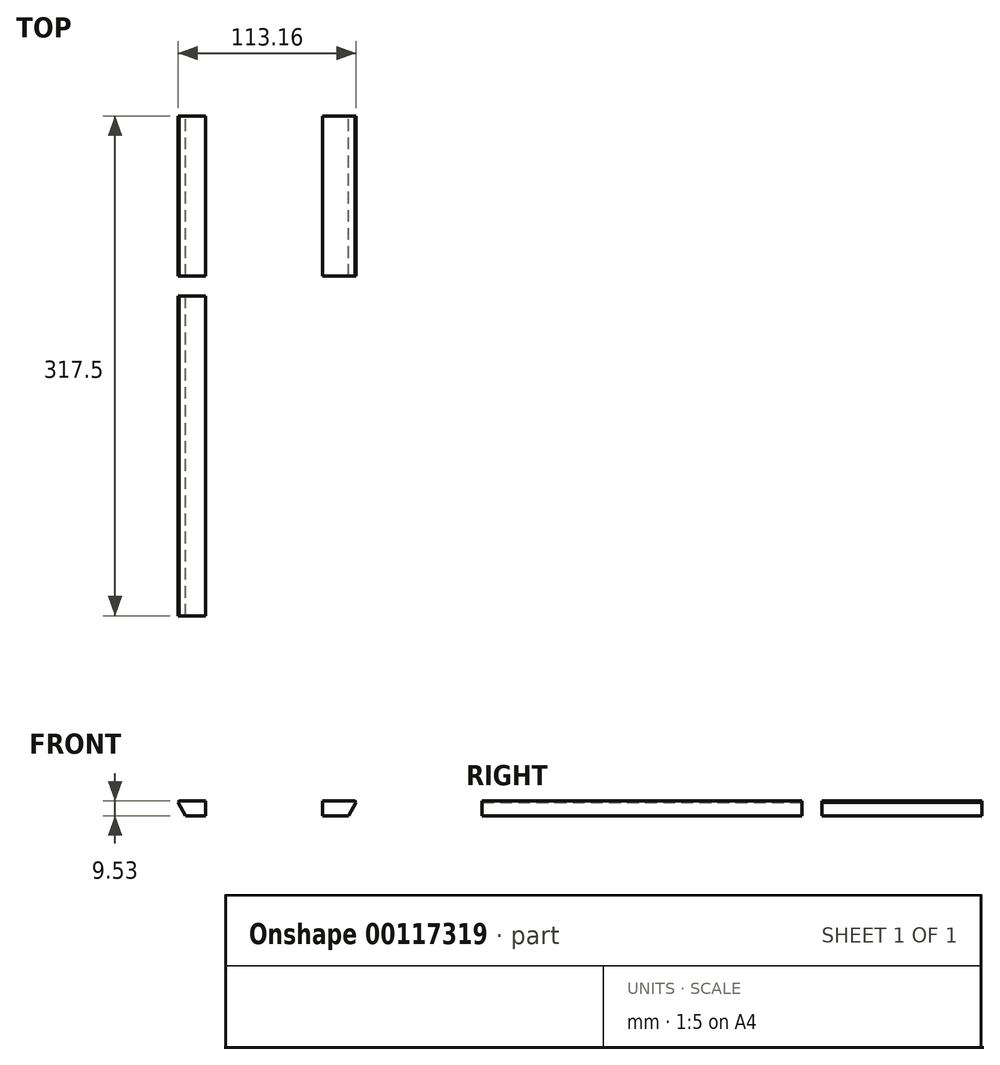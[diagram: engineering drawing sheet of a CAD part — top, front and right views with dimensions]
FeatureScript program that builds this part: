
annotation { "Feature Type Name" : "Feature", "Feature Type Description" : "" }
export const myFeature = defineFeature(function(context is Context, id is Id, definition is map)
    precondition{}
    {
        {
            var Q0;
            Q0=qCreatedBy(makeId("Front.planeOp"),FACE);
            var sketch = newSketch(context, id + "F0", { "sketchPlane" : qUnion([Q0])});
            skLineSegment(sketch, "E0.top", {"start": v(50.8, 6.35) * mm, "end": v(34.19, 6.35) * mm});
            skLineSegment(sketch, "E1", {"start": v(-52.63, 6.35) * mm, "end": v(-58.13, 15.87) * mm});
            skLineSegment(sketch, "E2", {"start": v(-58.13, 15.87) * mm, "end": v(-39.93, 15.87) * mm});
            skLineSegment(sketch, "E3", {"start": v(56.3, 15.88) * mm, "end": v(50.8, 6.35) * mm});
            skLineSegment(sketch, "E4", {"start": v(-39.93, 15.87) * mm, "end": v(-39.93, 6.35) * mm});
            skLineSegment(sketch, "E5", {"start": v(34.19, 15.88) * mm, "end": v(34.19, 6.35) * mm});
            skLineSegment(sketch, "E6.trimOffspring", {"start": v(-39.93, 6.35) * mm, "end": v(-52.63, 6.35) * mm});
            skLineSegment(sketch, "E7.trimOffspring", {"start": v(34.19, 15.88) * mm, "end": v(56.3, 15.88) * mm});
            skSolve(sketch);
        }
        {
            var Q0;
            Q0=makeQuery(id+"F0.imprint","IMPRINT",FACE,{"disambiguationData":[TD([[makeQuery(id+"F0.imprint","IMPRINT",EDGE,{"derivedFrom":sQuery(id+"F0.wireOp",EDGE,"E1")}),-1.0]])]});
            extrude(context, id + "F1", {"entities" : qUnion([Q0]), "depth" : 101.6 * mm});
        }
        {
            var Q0;
            Q0=makeQuery(id+"F0.imprint","IMPRINT",FACE,{"disambiguationData":[TD([[makeQuery(id+"F0.imprint","IMPRINT",EDGE,{"derivedFrom":sQuery(id+"F0.wireOp",EDGE,"E0.top")}),-1.0]])]});
            extrude(context, id + "F2", {"entities" : qUnion([Q0]), "depth" : 101.6 * mm});
        }
        {
            var Q0;
            Q0=makeQuery(id+"F1.opExtrude","SWEPT_EDGE",EDGE,{"disambiguationData":[OSD([sQuery(id+"F0.wireOp",EDGE,"E1"),sQuery(id+"F0.wireOp",EDGE,"E2")])]});
            var Q1;
            Q1=makeQuery(id+"F2.opExtrude","SWEPT_EDGE",EDGE,{"disambiguationData":[OSD([sQuery(id+"F0.wireOp",EDGE,"E3"),sQuery(id+"F0.wireOp",EDGE,"E7.trimOffspring")])]});
            chamfer(context, id + "F3", {"entities" : qUnion([Q0, Q1]), "chamferType" : ChamferType.TWO_OFFSETS, "width1" : 1.27 * mm, "oppositeDirection" : false, "width2" : 1.27 * mm, "tangentPropagation" : true});
        }
        {
            var Q0;
            Q0=makeQuery(id+"F1.opExtrude","CAP_FACE",FACE,{"disambiguationData":[OSD([sQuery(id+"F0.wireOp",EDGE,"E1"),sQuery(id+"F0.wireOp",EDGE,"E2"),sQuery(id+"F0.wireOp",EDGE,"E4"),sQuery(id+"F0.wireOp",EDGE,"E6.trimOffspring")])],"isStart":false});
            cPlane(context, id + "F4", {"entities" : qUnion([Q0]), "cplaneType" : CPlaneType.OFFSET, "offset" : 12.7 * mm, "width" : 152.4 * mm, "height" : 152.4 * mm});
        }
        {
            var Q0;
            Q0=qCreatedBy(id+"F4.planeOp",FACE);
            var sketch = newSketch(context, id + "F5", { "sketchPlane" : qUnion([Q0])});
            skLineSegment(sketch, "E8.0.0", {"start": v(-39.93, 15.87) * mm, "end": v(-56.86, 15.87) * mm});
            skLineSegment(sketch, "E8.0.1", {"start": v(-56.86, 15.87) * mm, "end": v(-57.5, 14.78) * mm});
            skLineSegment(sketch, "E8.0.2", {"start": v(-57.5, 14.78) * mm, "end": v(-52.63, 6.35) * mm});
            skLineSegment(sketch, "E8.0.3", {"start": v(-52.63, 6.35) * mm, "end": v(-39.93, 6.35) * mm});
            skLineSegment(sketch, "E8.0.4", {"start": v(-39.93, 6.35) * mm, "end": v(-39.93, 15.87) * mm});
            skSolve(sketch);
        }
        {
            var Q0;
            Q0=makeQuery(id+"F5.imprint","IMPRINT",FACE,{"disambiguationData":[TD([[makeQuery(id+"F5.imprint","IMPRINT",EDGE,{"derivedFrom":sQuery(id+"F5.wireOp",EDGE,"E8.0.0")}),1.0]])]});
            extrude(context, id + "F6", {"entities" : qUnion([Q0]), "depth" : 203.2 * mm});
        }
    });
